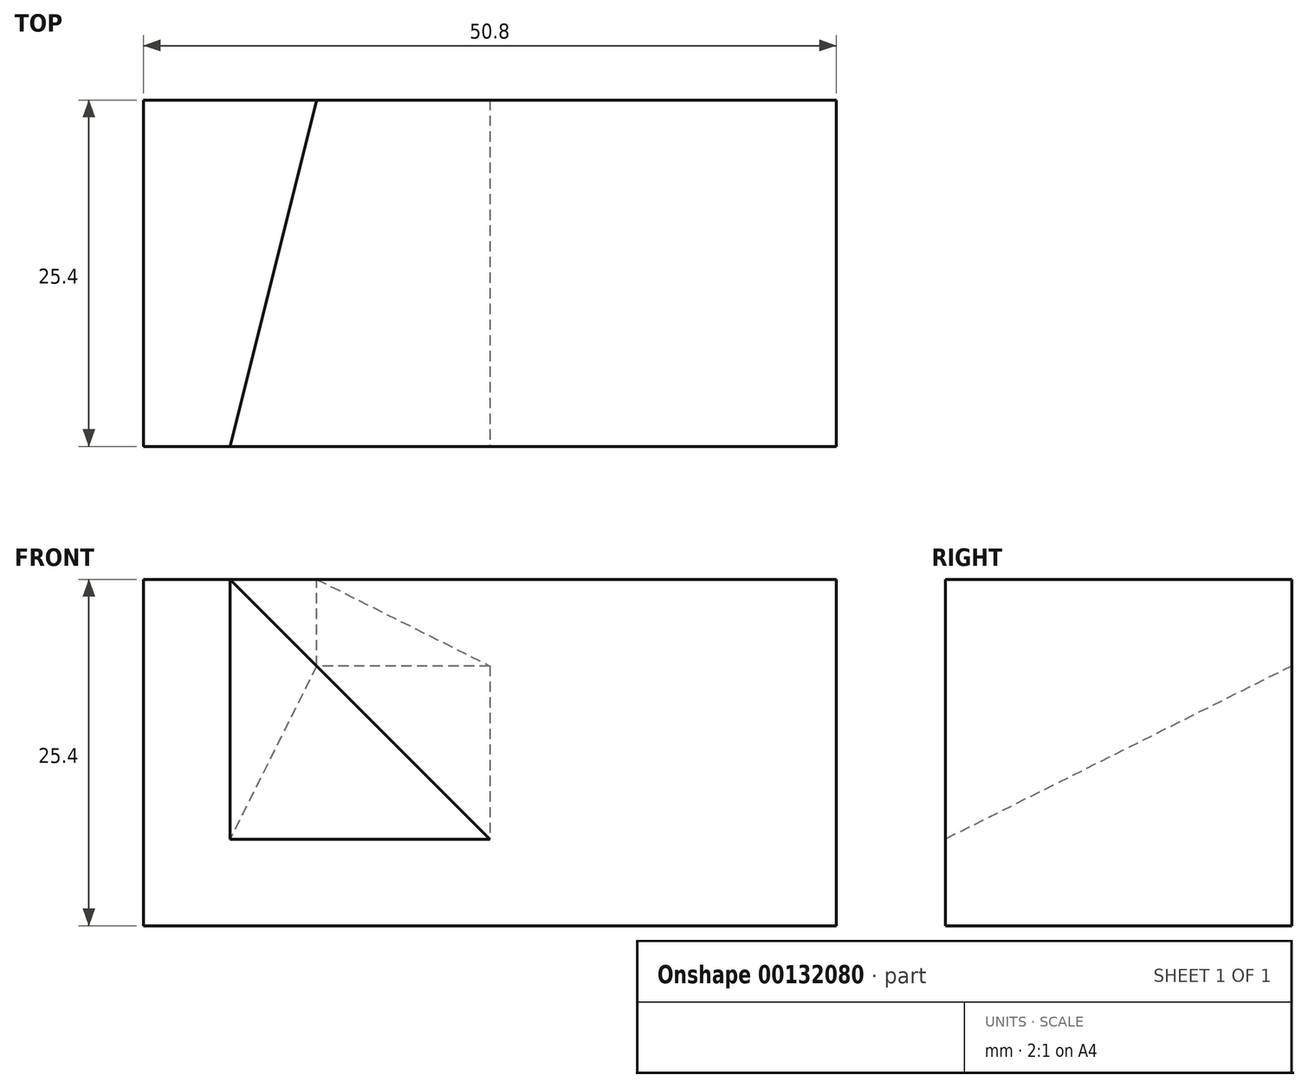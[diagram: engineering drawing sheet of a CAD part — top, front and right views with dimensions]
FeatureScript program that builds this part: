
annotation { "Feature Type Name" : "Feature", "Feature Type Description" : "" }
export const myFeature = defineFeature(function(context is Context, id is Id, definition is map)
    precondition{}
    {
        {
            var Q0;
            Q0=qCreatedBy(makeId("Front.planeOp"),FACE);
            var sketch = newSketch(context, id + "F0", { "sketchPlane" : qUnion([Q0])});
            skLineSegment(sketch, "E0", {"start": v(0, 0) * mm, "end": v(25.4, 0) * mm});
            skLineSegment(sketch, "E1", {"start": v(25.4, 0) * mm, "end": v(25.4, 6.35) * mm});
            skLineSegment(sketch, "E2", {"start": v(0, 0) * mm, "end": v(0, 25.4) * mm});
            skLineSegment(sketch, "E3", {"start": v(0, 25.4) * mm, "end": v(6.35, 25.4) * mm});
            skLineSegment(sketch, "E4", {"start": v(6.35, 25.4) * mm, "end": v(25.4, 6.35) * mm});
            skSolve(sketch);
        }
        {
            var Q0;
            Q0=qCreatedBy(makeId("Front.planeOp"),FACE);
            cPlane(context, id + "F1", {"entities" : qUnion([Q0]), "cplaneType" : CPlaneType.OFFSET, "offset" : 25.4 * mm, "oppositeDirection" : true, "width" : 152.4 * mm, "height" : 152.4 * mm});
        }
        {
            var Q0;
            Q0=qCreatedBy(id+"F1.planeOp",FACE);
            var sketch = newSketch(context, id + "F2", { "sketchPlane" : qUnion([Q0])});
            skLineSegment(sketch, "E5", {"start": v(0, 0) * mm, "end": v(0, 25.4) * mm});
            skLineSegment(sketch, "E6", {"start": v(0, 25.4) * mm, "end": v(12.7, 25.4) * mm});
            skLineSegment(sketch, "E7", {"start": v(0, 0) * mm, "end": v(25.4, 0) * mm});
            skLineSegment(sketch, "E8", {"start": v(25.4, 0) * mm, "end": v(25.4, 19.05) * mm});
            skLineSegment(sketch, "E9", {"start": v(25.4, 19.05) * mm, "end": v(12.7, 25.4) * mm});
            skSolve(sketch);
        }
        {
            var Q0;
            Q0=makeQuery(id+"F2.imprint","IMPRINT",FACE,{"disambiguationData":[TD([[makeQuery(id+"F2.imprint","IMPRINT",EDGE,{"derivedFrom":sQuery(id+"F2.wireOp",EDGE,"E5")}),-1.0]])]});
            var Q1;
            Q1=makeQuery(id+"F0.imprint","IMPRINT",FACE,{"disambiguationData":[TD([[makeQuery(id+"F0.imprint","IMPRINT",EDGE,{"derivedFrom":sQuery(id+"F0.wireOp",EDGE,"E0")}),1.0]])]});
            loft(context, id + "F3", {"sheetProfilesArray" : [{ "sheetProfileEntities" : qUnion([Q0]) }, { "sheetProfileEntities" : qUnion([Q1]) }]});
        }
        {
            var Q0;
            Q0=makeQuery(id+"F3.opLoft","SWEPT_BODY",BODY,{"disambiguationData":[OSD([makeQuery(id+"F0.imprint","IMPRINT",FACE,{"disambiguationData":[TD([[makeQuery(id+"F0.imprint","IMPRINT",EDGE,{"derivedFrom":sQuery(id+"F0.wireOp",EDGE,"E0")}),1.0]])]}),makeQuery(id+"F2.imprint","IMPRINT",FACE,{"disambiguationData":[TD([[makeQuery(id+"F2.imprint","IMPRINT",EDGE,{"derivedFrom":sQuery(id+"F2.wireOp",EDGE,"E5")}),-1.0]])]})])]});
            var Q1;
            Q1=makeQuery(id+"F3.opLoft","SWEPT_FACE",FACE,{"disambiguationData":[OSD([sQuery(id+"F0.wireOp",EDGE,"E0"),sQuery(id+"F0.wireOp",EDGE,"E1"),sQuery(id+"F0.wireOp",EDGE,"E4"),sQuery(id+"F2.wireOp",EDGE,"E7"),sQuery(id+"F2.wireOp",EDGE,"E8"),sQuery(id+"F2.wireOp",EDGE,"E9")])]});
            mirror(context, id + "F4", {"operationType" : NewBodyOperationType.ADD, "entities" : qUnion([Q0]), "mirrorPlane" : qUnion([Q1])});
        }
        {
            var Q0;
            Q0=qCreatedBy(makeId("Front.planeOp"),FACE);
            var sketch = newSketch(context, id + "F5", { "sketchPlane" : qUnion([Q0])});
            skLineSegment(sketch, "E10", {"start": v(6.35, 25.4) * mm, "end": v(25.4, 25.4) * mm});
            skLineSegment(sketch, "E11", {"start": v(25.4, 25.4) * mm, "end": v(25.4, 6.35) * mm});
            skLineSegment(sketch, "E12", {"start": v(6.35, 25.4) * mm, "end": v(25.4, 6.35) * mm});
            skSolve(sketch);
        }
        {
            var Q0;
            Q0=qCreatedBy(id+"F1.planeOp",FACE);
            var sketch = newSketch(context, id + "F6", { "sketchPlane" : qUnion([Q0])});
            skLineSegment(sketch, "E13", {"start": v(12.7, 25.4) * mm, "end": v(25.4, 25.4) * mm});
            skLineSegment(sketch, "E14", {"start": v(25.4, 25.4) * mm, "end": v(25.4, 19.05) * mm});
            skLineSegment(sketch, "E15", {"start": v(25.4, 19.05) * mm, "end": v(12.7, 25.4) * mm});
            skSolve(sketch);
        }
        {
            var Q1;
            Q1=makeQuery(id+"F6.imprint","IMPRINT",FACE,{"disambiguationData":[TD([[makeQuery(id+"F6.imprint","IMPRINT",EDGE,{"derivedFrom":sQuery(id+"F6.wireOp",EDGE,"E13")}),-1.0]])]});
            var Q2;
            Q2=makeQuery(id+"F5.imprint","IMPRINT",FACE,{"disambiguationData":[TD([[makeQuery(id+"F5.imprint","IMPRINT",EDGE,{"derivedFrom":sQuery(id+"F5.wireOp",EDGE,"E10")}),-1.0]])]});
            loft(context, id + "F7", {"sheetProfilesArray" : [{ "sheetProfileEntities" : qUnion([Q1]) }, { "sheetProfileEntities" : qUnion([Q2]) }]});
        }
        {
            var Q0;
            Q0=makeQuery(id+"F7.opLoft","SWEPT_BODY",BODY,{"disambiguationData":[OSD([makeQuery(id+"F5.imprint","IMPRINT",FACE,{"disambiguationData":[TD([[makeQuery(id+"F5.imprint","IMPRINT",EDGE,{"derivedFrom":sQuery(id+"F5.wireOp",EDGE,"E10")}),-1.0]])]}),makeQuery(id+"F6.imprint","IMPRINT",FACE,{"disambiguationData":[TD([[makeQuery(id+"F6.imprint","IMPRINT",EDGE,{"derivedFrom":sQuery(id+"F6.wireOp",EDGE,"E13")}),-1.0]])]})])]});
            var Q1;
            {var subQ0=sQuery(id+"F6.wireOp",EDGE,"E14");var subQ1=sQuery(id+"F6.wireOp",EDGE,"E15");var subQ2=sQuery(id+"F6.wireOp",EDGE,"E13");var subQ3=sQuery(id+"F5.wireOp",EDGE,"E11");var subQ4=sQuery(id+"F5.wireOp",EDGE,"E12");var subQ5=sQuery(id+"F5.wireOp",EDGE,"E10");Q1=makeQuery(id+"F7.opLoft","SWEPT_FACE",FACE,{"disambiguationData":[OSD([subQ5,subQ3,subQ4,subQ2,subQ0,subQ1]),TDD([makeQuery(id+"F5.imprint","INTERSECT",VERTEX,{"derivedFrom":[subQ5,subQ3]}),makeQuery(id+"F5.imprint","INTERSECT",VERTEX,{"derivedFrom":[subQ3,subQ4]}),makeQuery(id+"F5.imprint","IMPRINT",EDGE,{"derivedFrom":subQ3}),makeQuery(id+"F6.imprint","INTERSECT",VERTEX,{"derivedFrom":[subQ2,subQ0]}),makeQuery(id+"F6.imprint","INTERSECT",VERTEX,{"derivedFrom":[subQ0,subQ1]}),makeQuery(id+"F6.imprint","IMPRINT",EDGE,{"derivedFrom":subQ0})])]});}
            mirror(context, id + "F8", {"operationType" : NewBodyOperationType.ADD, "entities" : qUnion([Q0]), "mirrorPlane" : qUnion([Q1])});
        }
        {
            var Q0;
            {var subQ0=makeQuery(id+"F7.opLoft","CAP_FACE",FACE,{"disambiguationData":[OSD([makeQuery(id+"F5.imprint","IMPRINT",FACE,{"disambiguationData":[TD([[makeQuery(id+"F5.imprint","IMPRINT",EDGE,{"derivedFrom":sQuery(id+"F5.wireOp",EDGE,"E10")}),-1.0]])]})])],"isStart":true});Q0=makeQuery(id+"F8.boolean.opBoolean","MERGE",FACE,{"derivedFrom":[subQ0,makeQuery(id+"F8.opPattern","COPY",FACE,{"derivedFrom":subQ0,"instanceName":"1"})]});}
            var sketch = newSketch(context, id + "F9", { "sketchPlane" : qUnion([Q0])});
            skLineSegment(sketch, "E16", {"start": v(6.35, 25.4) * mm, "end": v(6.35, 6.35) * mm});
            skLineSegment(sketch, "E17", {"start": v(6.35, 6.35) * mm, "end": v(25.4, 6.35) * mm});
            skLineSegment(sketch, "E18", {"start": v(25.4, 6.35) * mm, "end": v(6.35, 25.4) * mm});
            skSolve(sketch);
        }
        {
            var Q0;
            {var subQ0=makeQuery(id+"F7.opLoft","CAP_FACE",FACE,{"disambiguationData":[OSD([makeQuery(id+"F6.imprint","IMPRINT",FACE,{"disambiguationData":[TD([[makeQuery(id+"F6.imprint","IMPRINT",EDGE,{"derivedFrom":sQuery(id+"F6.wireOp",EDGE,"E13")}),-1.0]])]})])],"isStart":true});Q0=makeQuery(id+"F8.boolean.opBoolean","MERGE",FACE,{"derivedFrom":[subQ0,makeQuery(id+"F8.opPattern","COPY",FACE,{"derivedFrom":subQ0,"instanceName":"1"})]});}
            var sketch = newSketch(context, id + "F10", { "sketchPlane" : qUnion([Q0])});
            skLineSegment(sketch, "E19", {"start": v(-12.7, 25.4) * mm, "end": v(-25.4, 19.05) * mm});
            skLineSegment(sketch, "E20", {"start": v(-25.4, 19.05) * mm, "end": v(-12.7, 19.05) * mm});
            skLineSegment(sketch, "E21", {"start": v(-12.7, 19.05) * mm, "end": v(-12.7, 25.4) * mm});
            skSolve(sketch);
        }
        {
            var Q0;
            Q0=makeQuery(id+"F10.imprint","IMPRINT",FACE,{"disambiguationData":[TD([[makeQuery(id+"F10.imprint","IMPRINT",EDGE,{"derivedFrom":sQuery(id+"F10.wireOp",EDGE,"E19")}),1.0]])]});
            var Q1;
            Q1=makeQuery(id+"F9.imprint","IMPRINT",FACE,{"disambiguationData":[TD([[makeQuery(id+"F9.imprint","IMPRINT",EDGE,{"derivedFrom":sQuery(id+"F9.wireOp",EDGE,"E16")}),1.0]])]});
            loft(context, id + "F11", {"sheetProfilesArray" : [{ "sheetProfileEntities" : qUnion([Q0]) }, { "sheetProfileEntities" : qUnion([Q1]) }]});
        }
    });
